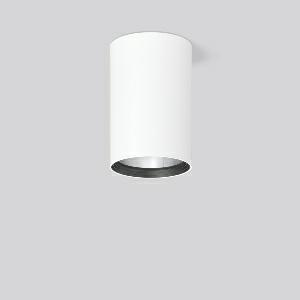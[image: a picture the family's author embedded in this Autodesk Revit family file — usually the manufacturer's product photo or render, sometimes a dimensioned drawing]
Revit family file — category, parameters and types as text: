
# Revit family: heledon_maxi_a_931225_002_3_76_9714
name_source: partatom
category: Lighting Fixtures
units: mm (PartAtom-declared; Revit-internal decimal feet)

## family parameters
Cut with Voids When Loaded = No
Host = Face
Light Source = No
Part Type = Normal
Room Calculation Point = No
Round Connector Dimension = Use Diameter
Shared = No

## types (1)
- HELEDON maxi A (1 x LED Modul 935, 4400 lm, 3500)
    Apparent Load = 35 VA
    Approval mark = CE
    CIE Flux Codes = 100 100 100 100 100
    Color Rendering = 92
    Color Temperature = 3500
    Default Elevation = 1800 mm
    Description = Series: HELEDON maxi
Cylindrical surface-mounted downlight. Housing: die-cast aluminium, powder-coated. Internal ceiling frame polycarbonate with bayonet mounting. Black plastic ring and recessed LED to prevent glare from the side. Optical assembly with reflector made of MIRO-Silver with 98% total light reflection for outstanding efficiency - can be changed without tools. Best colour rendering index Ra>90. Suitable for Ceiling mounting. Easy installation with a separate ceiling frame with bayonet mounting and plug connection. Driver integrated. Connected via plug-in connector. High quality converter without flickering and stroboscopic effect. The following accessories can be mounted without use of tools: interchangeable lenses, decorative glasses, honeycomb louvre, clear and frosted diffusers, white interchangeable plastic ring. 
Colour: traffic white, matt (RAL 9016)
Diameter: 123 mm
Height: 183 mm
Lamp: LED
Socket: without socket
Colour temperature: 3500K
Colour rendering index (CRI): 92
System power: 35 W
Rated luminous flux: 4400 lm
Luminous efficiency: 126 lm/W
Control gear: Converter, dimmable, DALI
Protection class: I
Type of protection: IP 20
    Height = 183 mm
    Lamp = 1 x LED Modul 935
    Lamp Light Flux = 4400 lm
    Lamp count = 1
    Length = 123 mm
    Lifetime = 50000 h
    Luminous efficacy = 126 lm/W
    Manufacturer = RZB
    ModVariant = No
    Model = 931225.002.3.76
    Mounting Place = Ceiling
    Mounting Type = Surface mounted
    Number of Poles = 1
    OnlyDefault = Yes
    Power Factor = 1
    Product Name = HELEDON maxi A
    Product group = Surface mounted downlights
    ProductGroupID = 302
    Protection Class = Protection class I
    Protection Degree = IP 20
    RLX_Detail_Level = 1
    RLX_Emergency_Light_Flux = 0 lm
    RLX_Emergency_Type = 0
    RLX_Emergency_Type_DB = No
    RlxData = <blob elided: 96289 chars, md5=cc8cf93a>
    Socket = socket
    Standby Power = 0 W
    System Light Flux = 4400 lm
    System Power = 35 W
    Type Comments = Product without accessories
    Type Image = 931192.002.jpg
    URL = http://relux.com
    VarID = ---
    Voltage = 230 V
    Voltage Range = 220-240 V
    Weight = 0.00 kg
    Width = 0 mm  [stored 0 ft]

note: [stored X ft] marks values corroborated as IEEE doubles in the binary element streams (Revit-internal decimal feet)

## geometry (parser evidence)
native form markers: Blend x4, Sweep x9
no freeform markers — native parametric forms only
